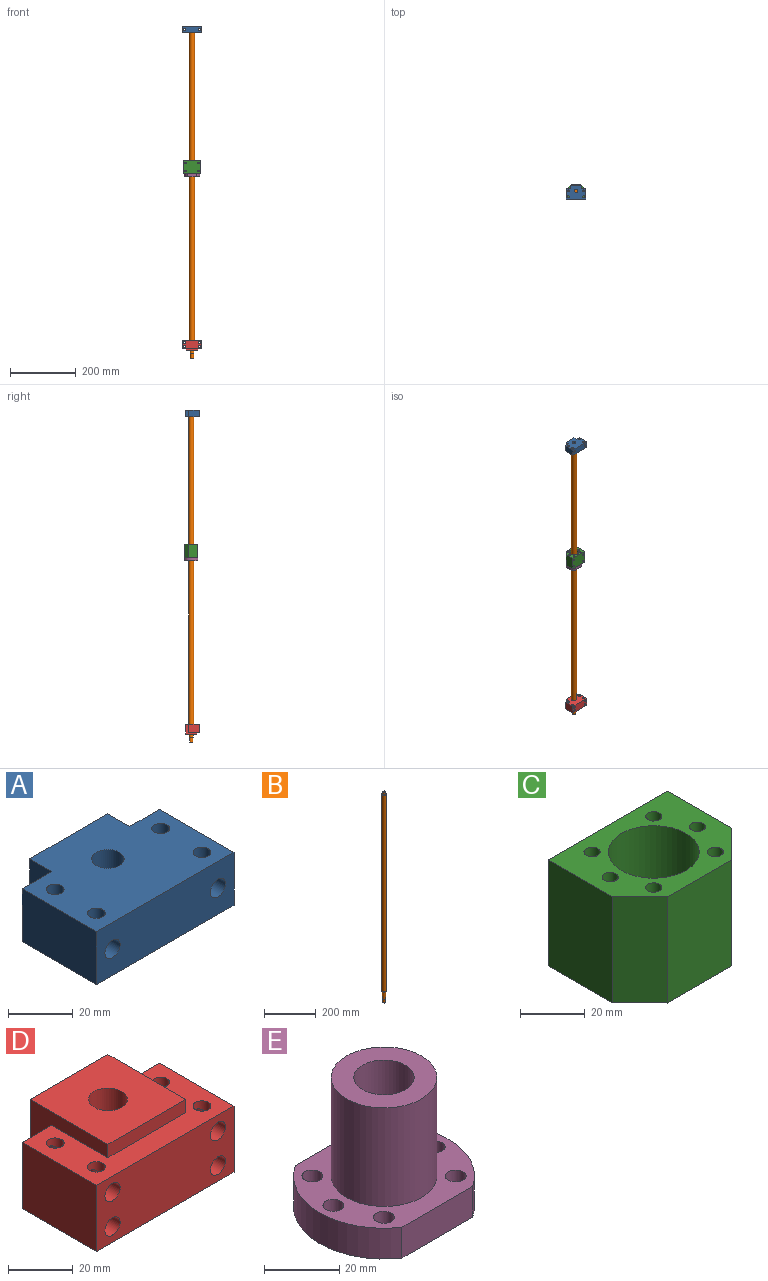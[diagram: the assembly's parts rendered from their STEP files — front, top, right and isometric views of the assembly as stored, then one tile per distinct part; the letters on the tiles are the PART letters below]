
ASSEMBLY  parts=5 mates=10
PART A: 25 faces, bbox 60x42.1x20 mm
  f0: cylinder r=3.3mm len=31mm, axis (0,1,0), area 535.9mm2, adj f2,f5,f8,f13,f18,f24
  f1: cylinder r=3.3mm len=31mm, axis (0,1,0), area 535.9mm2, adj f3,f4,f8,f14,f15,f22
  f2: cylinder r=2.75mm len=8.18mm, axis (0,0,-1), area 127.6mm2, adj f0,f19
  f3: cylinder r=2.75mm len=8.18mm, axis (0,0,-1), area 127.6mm2, adj f1,f19
  f4: cylinder r=2.75mm len=8.18mm, axis (0,0,-1), area 127.6mm2, adj f1,f19
  f5: cylinder r=2.75mm len=8.18mm, axis (0,0,-1), area 127.6mm2, adj f0,f19
  f6: plane 20x13mm, normal (0,1,0), area 168.4mm2, adj f7,f17,f19,f20,f23
  f7: plane 32.5x20mm, normal (-1,0,0), area 650mm2, adj f6,f8,f19,f20
  f8: plane 60x20mm, normal (0,-1,0), area 1131.6mm2, adj f0,f1,f7,f9,f19,f20
  f9: plane 32.5x20mm, normal (1,0,0), area 650mm2, adj f8,f10,f19,f20
  f10: plane 20x13mm, normal (0,1,0), area 168.4mm2, adj f9,f11,f19,f20,f21
  f11: plane 20x9.61mm, normal (1,0,0), area 192.2mm2, adj f10,f12,f19,f20
  f12: plane 34x20mm, normal (0,1,0), area 680mm2, adj f11,f17,f19,f20
  f13: cylinder r=2.75mm len=8.18mm, axis (0,0,-1), area 127.6mm2, adj f0,f20
  f14: cylinder r=2.75mm len=8.18mm, axis (0,0,-1), area 127.6mm2, adj f1,f20
  f15: cylinder r=2.75mm len=8.18mm, axis (0,0,-1), area 127.6mm2, adj f1,f20
  f16: cylinder r=5mm len=20mm, axis (0,0,-1), area 628.3mm2, adj f19,f20
  f17: plane 20x9.61mm, normal (-1,0,0), area 192.2mm2, adj f6,f12,f19,f20
  f18: cylinder r=2.75mm len=8.18mm, axis (0,0,-1), area 127.6mm2, adj f0,f20
  f19: plane 60x42.11mm, normal (0,0,1), area 2103.2mm2, adj f2,f3,f4,f5,f6,f7,f8,f9
  f20: plane 60x42.11mm, normal (0,0,-1), area 2103.2mm2, adj f6,f7,f8,f9,f10,f11,f12,f13
  f21: cylinder r=5.4mm len=10.8mm, axis (0,1,0), area 50.9mm2, adj f10,f22
  f22: plane 10.8x10.8mm, normal (0,1,0), area 57.4mm2, adj f1,f21
  f23: cylinder r=5.4mm len=10.8mm, axis (0,1,0), area 50.9mm2, adj f6,f24
  f24: plane 10.8x10.8mm, normal (0,1,0), area 57.4mm2, adj f0,f23
PART B: 9 faces, bbox 16x16x1000 mm
  f0: cylinder r=5mm len=11mm, axis (0,0,-1), area 345.6mm2, adj f1,f2
  f1: plane 10x10mm, normal (0,0,1), area 78.5mm2, adj f0
  f2: plane 16x16mm, normal (0,0,1), area 122.5mm2, adj f0,f4
  f3: plane 16x16mm, normal (0,0,-1), area 88mm2, adj f4,f5
  f4: cylinder r=8mm len=935mm, axis (0,0,-1), area 46998.2mm2, adj f2,f3
  f5: cylinder r=6mm len=39mm, axis (0,0,-1), area 1470.3mm2, adj f3,f6
  f6: plane 12x12mm, normal (0,0,-1), area 34.6mm2, adj f5,f8
  f7: plane 10x10mm, normal (0,0,-1), area 78.5mm2, adj f8
  f8: cylinder r=5mm len=15mm, axis (0,0,-1), area 471.2mm2, adj f6,f7
PART C: 23 faces, bbox 52x40x40 mm
  f0: plane 52x40mm, normal (0,1,0), area 2001.5mm2, adj f1,f11,f13,f14,f15,f17,f19,f21
  f1: plane 40x28mm, normal (-1,0,0), area 1120mm2, adj f0,f2,f13,f14
  f2: plane 40x12mm, normal (-0.71,-0.71,0), area 678.8mm2, adj f1,f3,f13,f14
  f3: plane 40x28mm, normal (0,-1,0), area 1120mm2, adj f2,f4,f13,f14
  f4: plane 40x12mm, normal (0.71,-0.71,0), area 678.8mm2, adj f3,f11,f13,f14
  f5: cylinder r=2.5mm len=40mm, axis (0,0,-1), area 628.3mm2, adj f13,f14
  f6: cylinder r=2.5mm len=40mm, axis (0,0,-1), area 628.3mm2, adj f13,f14
  f7: cylinder r=2.5mm len=40mm, axis (0,0,-1), area 628.3mm2, adj f13,f14
  f8: cylinder r=2.5mm len=40mm, axis (0,0,-1), area 628.3mm2, adj f13,f14
  f9: cylinder r=2.5mm len=40mm, axis (0,0,-1), area 628.3mm2, adj f13,f14
  f10: cylinder r=14mm len=40mm, axis (0,0,-1), area 3518.6mm2, adj f13,f14
  f11: plane 40x28mm, normal (1,0,0), area 1120mm2, adj f0,f4,f13,f14
  f12: cylinder r=2.5mm len=40mm, axis (0,0,-1), area 628.3mm2, adj f13,f14
  f13: plane 52x40mm, normal (0,0,1), area 1202.4mm2, adj f0,f1,f2,f3,f4,f5,f6,f7
  f14: plane 52x40mm, normal (0,0,-1), area 1202.4mm2, adj f0,f1,f2,f3,f4,f5,f6,f7
  f15: cylinder r=2.5mm len=15mm, axis (0,1,0), area 235.6mm2, adj f0,f16
  f16: plane 5x5mm, normal (0,1,0), area 19.6mm2, adj f15
  f17: cylinder r=2.5mm len=15mm, axis (0,1,0), area 235.6mm2, adj f0,f18
  f18: plane 5x5mm, normal (0,1,0), area 19.6mm2, adj f17
  f19: cylinder r=2.5mm len=15mm, axis (0,1,0), area 235.6mm2, adj f0,f20
  f20: plane 5x5mm, normal (0,1,0), area 19.6mm2, adj f19
  f21: cylinder r=2.5mm len=15mm, axis (0,1,0), area 235.6mm2, adj f0,f22
  f22: plane 5x5mm, normal (0,1,0), area 19.6mm2, adj f21
PART D: 37 faces, bbox 60x42x30 mm
  f0: cylinder r=3.3mm len=31mm, axis (0,1,0), area 535.9mm2, adj f14,f17,f18,f25,f26,f36
  f1: cylinder r=3.3mm len=31mm, axis (0,1,0), area 535.9mm2, adj f6,f7,f14,f25,f26,f34
  f2: cylinder r=3.3mm len=31mm, axis (0,1,0), area 535.9mm2, adj f4,f5,f14,f27,f28,f32
  f3: cylinder r=3.3mm len=31mm, axis (0,1,0), area 535.9mm2, adj f14,f15,f16,f27,f28,f30
  f4: cylinder r=2.75mm len=5.5mm, axis (0,0,-1), area 58.5mm2, adj f2,f21
  f5: cylinder r=2.75mm len=5.5mm, axis (0,0,-1), area 58.5mm2, adj f2,f21
  f6: cylinder r=2.75mm len=5.5mm, axis (0,0,-1), area 58.5mm2, adj f1,f21
  f7: cylinder r=2.75mm len=5.5mm, axis (0,0,-1), area 58.5mm2, adj f1,f21
  f8: plane 25x13mm, normal (0,1,0), area 141.8mm2, adj f9,f19,f21,f22,f29,f31
  f9: plane 34x30mm, normal (1,0,0), area 407.5mm2, adj f8,f10,f21,f22,f23,f24
  f10: plane 34x30mm, normal (0,1,0), area 1020mm2, adj f9,f11,f22,f23
  f11: plane 34x30mm, normal (-1,0,0), area 407.5mm2, adj f10,f12,f21,f22,f23,f24
  f12: plane 25x13mm, normal (0,1,0), area 141.8mm2, adj f11,f13,f21,f22,f33,f35
  f13: plane 32.5x25mm, normal (-1,0,0), area 812.5mm2, adj f12,f14,f21,f22
  f14: plane 60x25mm, normal (0,-1,0), area 1363.2mm2, adj f0,f1,f2,f3,f13,f19,f21,f22
  f15: cylinder r=2.75mm len=5.5mm, axis (0,0,-1), area 58.5mm2, adj f3,f22
  f16: cylinder r=2.75mm len=5.5mm, axis (0,0,-1), area 58.5mm2, adj f3,f22
  f17: cylinder r=2.75mm len=5.5mm, axis (0,0,-1), area 58.5mm2, adj f0,f22
  f18: cylinder r=2.75mm len=5.5mm, axis (0,0,-1), area 58.5mm2, adj f0,f22
  f19: plane 32.5x25mm, normal (1,0,0), area 812.5mm2, adj f8,f14,f21,f22
  f20: cylinder r=6mm len=30mm, axis (0,0,-1), area 1131mm2, adj f22,f23
  f21: plane 60x32.5mm, normal (0,0,1), area 1022mm2, adj f4,f5,f6,f7,f8,f9,f11,f12
  f22: plane 60x42mm, normal (0,0,-1), area 2064.9mm2, adj f8,f9,f10,f11,f12,f13,f14,f15
  f23: plane 34x34mm, normal (0,0,1), area 1042.9mm2, adj f9,f10,f11,f20,f24
  f24: plane 34x5mm, normal (0,-1,0), area 170mm2, adj f9,f11,f21,f23
  f25: cylinder r=2.75mm len=9.35mm, axis (0,0,-1), area 134.2mm2, adj f0,f1
  f26: cylinder r=2.75mm len=9.35mm, axis (0,0,-1), area 134.2mm2, adj f0,f1
  f27: cylinder r=2.75mm len=9.35mm, axis (0,0,-1), area 134.2mm2, adj f2,f3
  f28: cylinder r=2.75mm len=9.35mm, axis (0,0,-1), area 134.2mm2, adj f2,f3
  f29: cylinder r=5.4mm len=10.8mm, axis (0,1,0), area 50.9mm2, adj f8,f30
  f30: plane 10.8x10.8mm, normal (0,1,0), area 57.4mm2, adj f3,f29
  f31: cylinder r=5.4mm len=10.8mm, axis (0,1,0), area 50.9mm2, adj f8,f32
  f32: plane 10.8x10.8mm, normal (0,1,0), area 57.4mm2, adj f2,f31
  f33: cylinder r=5.4mm len=10.8mm, axis (0,1,0), area 50.9mm2, adj f12,f34
  f34: plane 10.8x10.8mm, normal (0,1,0), area 57.4mm2, adj f1,f33
  f35: cylinder r=5.4mm len=10.8mm, axis (0,1,0), area 50.9mm2, adj f12,f36
  f36: plane 10.8x10.8mm, normal (0,1,0), area 57.4mm2, adj f0,f35
PART E: 15 faces, bbox 48x40x42 mm
  f0: plane 26.53x10mm, normal (0,1,0), area 265.3mm2, adj f1,f3,f11,f12
  f1: cylinder r=24mm len=40mm, axis (0,0,-1), area 472.9mm2, adj f0,f2,f11,f12
  f2: plane 26.53x10mm, normal (0,-1,0), area 265.3mm2, adj f1,f3,f11,f12
  f3: cylinder r=24mm len=40mm, axis (0,0,-1), area 472.9mm2, adj f0,f2,f11,f12
  f4: cylinder r=2.75mm len=10mm, axis (0,0,-1), area 172.8mm2, adj f11,f12
  f5: cylinder r=2.75mm len=10mm, axis (0,0,-1), area 172.8mm2, adj f11,f12
  f6: cylinder r=2.75mm len=10mm, axis (0,0,-1), area 172.8mm2, adj f11,f12
  f7: cylinder r=2.75mm len=10mm, axis (0,0,-1), area 172.8mm2, adj f11,f12
  f8: cylinder r=2.75mm len=10mm, axis (0,0,-1), area 172.8mm2, adj f11,f12
  f9: cylinder r=2.75mm len=10mm, axis (0,0,-1), area 172.8mm2, adj f11,f12
  f10: cylinder r=8mm len=42mm, axis (0,0,-1), area 2111.2mm2, adj f12,f14
  f11: plane 48x40mm, normal (0,0,1), area 907.2mm2, adj f0,f1,f2,f3,f4,f5,f6,f7
  f12: plane 48x40mm, normal (0,0,-1), area 1321.9mm2, adj f0,f1,f2,f3,f4,f5,f6,f7
  f13: cylinder r=14mm len=32mm, axis (0,0,-1), area 2814.9mm2, adj f11,f14
  f14: plane 28x28mm, normal (0,0,1), area 414.7mm2, adj f10,f13
PLACE A t=(-108.07,-149.73,1921.5)mm
PLACE B t=(-2.27,-0.45,932.5)mm
PLACE C rot(axis=(1,0,0),180deg) t=(-120.9,55.75,1533)mm
PLACE D rot(axis=(0,1,0),180deg) t=(-87.39,-145.6,986.5)mm
PLACE E t=(-19.88,74.23,1483)mm
MATE cylindrical D.f20 <-> B.f0  axis (0,0,1) through (-51.13,34.99,986.5)mm
MATE planar C.f13 <-> E.f1  axis (0,0,-1) through (-51.13,33.07,1493)mm
MATE cylindrical E.f5 <-> C.f7  axis (0,0,-1) through (-64.57,48.42,1488)mm
MATE planar D.f14 <-> A.f8  axis (0,-1,0) through (-51.13,9.99,974)mm
MATE cylindrical C.f10 <-> E.f1  axis (0,0,1) through (-51.13,34.99,1493)mm
MATE cylindrical A.f16 <-> B.f0  axis (0,0,-1) through (-51.13,34.99,1921.5)mm
MATE planar D.f22 <-> B.f0  axis (0,0,1) through (-51.13,29.05,986.5)mm
MATE cylindrical E.f1 <-> B.f0  axis (0,0,-1) through (-51.13,34.99,1504)mm
MATE planar A.f20 <-> B.f0  axis (0,0,-1) through (-51.13,29.19,1921.5)mm
MATE cylindrical E.f9 <-> C.f6  axis (0,0,-1) through (-37.7,48.42,1488)mm
